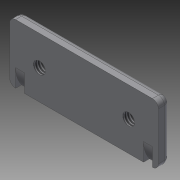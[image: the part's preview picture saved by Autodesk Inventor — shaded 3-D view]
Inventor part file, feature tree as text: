
AUTODESK INVENTOR PART (.ipt)
format: ipt  version: 2013 (Build 170138000, 138)  size: 119,808 bytes
history: native  units: mm
features: sketch x3, extrude x1, hole x1, plane x1, revolve x1, fillet x1, mirror x1
ambient origin geometry x8: Origin, YZ Plane, XZ Plane, XY Plane, X Axis, Y Axis, Z Axis, Center Point
bodies: Solid1 (feature_tree)
feature tree (9):
  extrude  "Extrusion1"  Depth=25.0mm
  hole  "Hole1"  [1 undecoded]
  plane  "Work Plane1"
  revolve  "Revolution1"  [1 undecoded]
  fillet  "Fillet1"  [1 undecoded]
  mirror  "Mirror1"
  sketch  "Sketch1"  dims[d0=10.0mm d2=25.0mm]
  sketch  "Sketch2"  dims[d3=2.0mm d4=0.0mm d5=5.0mm]
  sketch  "Sketch4"  dims[d6=2.013mm d7=6.0mm d8=4.0mm d9=2.0mm d10=90.0deg d11=8.0mm d12=20.594885mm d13=1.0mm d14=-5.0mm d15=3.0mm d16=5.0mm d17=5.0mm d18=1.5mm d19=1.0mm d20=90.0deg]
note: 3 required parameter values undecoded (feature->parameter linkage not recoverable at this tier; creation-order binding heuristic only, values carry confidence <= 0.55)